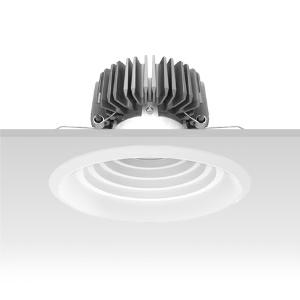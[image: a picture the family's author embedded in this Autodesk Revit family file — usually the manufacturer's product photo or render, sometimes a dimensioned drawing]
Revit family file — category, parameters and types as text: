
# Revit family: 3f_filippi_-_3f_reno_bianco_ampio_3f_filippi_-_30633_-_3f_reno_200_wh_3000-930_wide
name_source: partatom
category: Lighting Fixtures
units: mm (PartAtom-declared; Revit-internal decimal feet)

## family parameters
Cut with Voids When Loaded = No
Host = Face
Light Source = No
Part Type = Normal
Room Calculation Point = No
Round Connector Dimension = Use Diameter
Shared = No

## types (1)
- 3F Filippi - 3F Reno Bianco Ampio (1 x LED, 2644 lm, 37 W, 3000 K)
    Apparent Load = 37 VA
    Approval mark = CE
    CIE Flux Codes = 80 97 100 100 100
    Color Rendering = 90
    Color Temperature = 3000 K
    Control Gear = Electronic ballast
    Default Elevation = 1800 mm
    Description = ILLUMINOTECHNICAL
Luminous efficiency 100% (DLOR 100%, ULOR 0%).
Initial luminous flux of the luminaire 2644 lm.
Direct symmetric wide distribution.
Installation Interdistance Transv.D = 1.56 x hu - Long.D = 1.56 x hu.
Tabular UGR (CIE 117 - 4H-8H; S=0.25H; 70/50/20): RUG 20.4 - 20.4.
Beam angle: 85° - 84°.
Luminous efficacy 71 lm/W.
Lifetime (L90/B10): 30000 h. (tq+25°C)
Lifetime (L85/B10): 50000 h. (tq+25°C)
Lifetime (L70/B10): 80000 h. (tq+25°C)
Sudden decreased luminous flux after 50000 hours: 0% (C0).
Photobiological safety in compliance with IEC/TR 62778: RG0 risk exempt, (IEC 62471).
In compliance with IEC/EN 62722-2-1 - IEC/EN 62717 standards.

SOURCE
Compact LED module 3000/930.
Energy efficiency class (UE 2019/2020 - UE 2019/2015): E.
CIE 13.3 Colour rendering index: CRI >90 (R9 >50%).
IES TM-30 Fidelity Index: Rf = 92 Rg = 101.
CCT nominal colour temperature 3000 K.
Colour initial tolerance (MacAdam): SDCM 3.
Zhaga Book 3 compliant.

MECHANICAL
Passive heat dissipator in die-casting aluminium, oversized, for optimum thermal management of the LED module.
Parabolic element with graduated/concentric rings in white polycarbonate.
Transparent external lens with glossy and satin differentiated surfaces, with a cooling and anti-insect system in methacrylate (PMMA).
Fastening spring clips in stainless steel.
Dimensions: diameter 216 mm, height 142 mm. Weight 1.445 kg.
IP44 protection degree for exposed part, IP20 for recessed part.
Mechanical strength to impacts IK04 (0.5 joule).
Glow-wire test resistance 650°C.

ELECTRICAL
Wiring on a separate unit.
Halogen Free electronic wiring 230V-50/60Hz, power factor 0.95, THD <25%, constant output current, SELV, class II, 1 driver.
Power of the luminaire 37 W.
ENEC - CE.
SAFE FLICKER: PstLM=<1 and SVM=<0.4 (IEC TR 61547-1 and IEC TR 63158), to ensure a more comfortable and safe light.
Luminaire compliant with EN 60598-2-22 for power supply from a centralised emergency system CPSS (Central Power Supply System), not incorporated in the luminaire - high risk areas excluded. The default power and flux are 100% in AC and 100% in DC.
Ambient temperature from 0°C to +25°C.
Temperature class T6 max 85°C.
Relative humidity UR: <85%.

INSTALLATION
Pull-up recessed fitting.
False ceiling carving: 200 mm.
All accessories dedicated to this product are available on the Catalog and on our website www.3F-Filippi.com.

APPLICATIONS
Environments: architectural, commercial, exhibition areas, transit areas, corridors, shops, display windows, service areas.
In false ceilings with narrow voids.

WARNING
Luminaire designed for disposal/recycling at end-of-life.
Replaceable (LED only) light source by a professional. Replaceable control gear by a professional.
    Height = 0 mm  [stored 0 ft]
    Lamp = 1 x LED
    Lamp Light Flux = 2644 lm
    Lamp Power = 37 W
    Lamp count = 1
    Length = 216 mm
    Lifetime = 50000 h
    Luminous efficacy = 71 lm/W
    Manufacturer = 3F Filippi
    ModVariant = No
    Model = 3F Filippi - 30633 - 3F Reno 200 WH 3000-930 WIDE
    Mounting Place = Ceiling
    Mounting Type = Recessed
    Number of Poles = 1
    OnlyDefault = Yes
    Power Factor = 1
    Product Name = 3F Filippi - 3F Reno Bianco Ampio
    Product group = recessed luminaire
    ProductGroupID = 4
    Protection Class = Protection class II
    Protection Degree = IP 20
    RLX_Detail_Level = 1
    RLX_Emergency_Light_Flux = 0 lm
    RLX_Emergency_Type = 0
    RLX_Emergency_Type_DB = No
    RlxData = <blob elided: 92001 chars, md5=964d1638>
    Socket = socket
    Standby Power = 0 W
    System Light Flux = 2644 lm
    System Power = 37 W
    Type Comments = Product without accessories
    Type Image = 3ffilippi_3f_reno_200_wh_2500_3000_4000.jpg
    URL = http://relux.com
    VarID = ---
    Voltage = 0 V
    Weight = 0.00 kg
    Width = 0 mm  [stored 0 ft]

note: [stored X ft] marks values corroborated as IEEE doubles in the binary element streams (Revit-internal decimal feet)

## geometry (parser evidence)
native form markers: Blend x4, Sweep x11
no freeform markers — native parametric forms only
